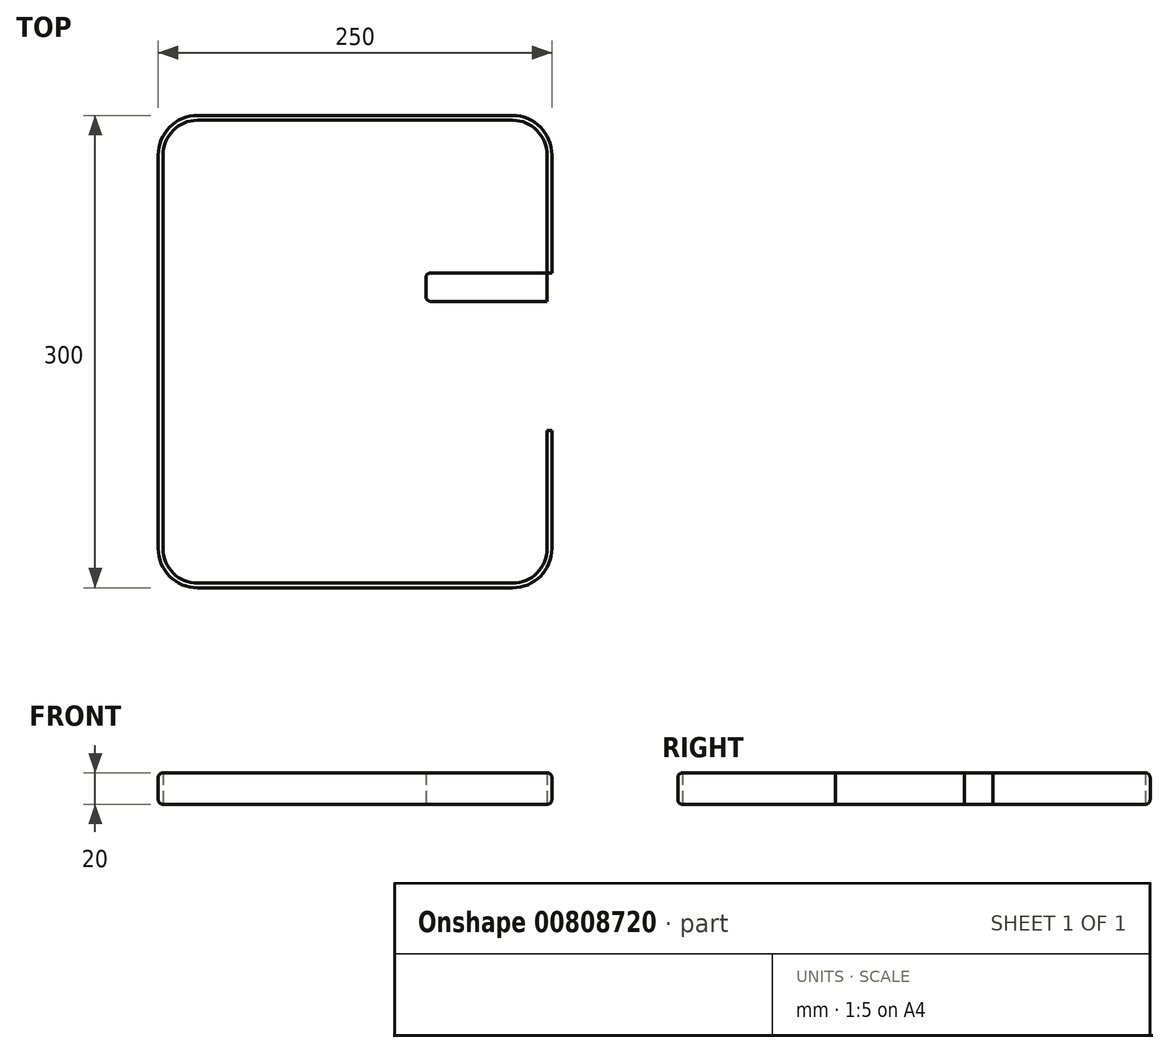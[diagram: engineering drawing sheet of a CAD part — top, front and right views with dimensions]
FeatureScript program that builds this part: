
annotation { "Feature Type Name" : "Feature", "Feature Type Description" : "" }
export const myFeature = defineFeature(function(context is Context, id is Id, definition is map)
    precondition{}
    {
        {
            var Q0;
            Q0=qCreatedBy(makeId("Top.planeOp"),FACE);
            var sketch = newSketch(context, id + "F0", { "sketchPlane" : qUnion([Q0])});
            skLineSegment(sketch, "E0.bottom", {"start": v(100, -150) * mm, "end": v(-100, -150) * mm});
            skLineSegment(sketch, "E0.top", {"start": v(100, 150) * mm, "end": v(-100, 150) * mm});
            skLineSegment(sketch, "E0.left", {"start": v(125, -125) * mm, "end": v(125, 125) * mm});
            skLineSegment(sketch, "E0.right", {"start": v(-125, -125) * mm, "end": v(-125, 125) * mm});
            skPoint(sketch, "E0.middle", {"position": v(0, 0) * mm});
            skPoint(sketch, "E1.visualSharp", {"position": v(-125, 150) * mm});
            skArc(sketch, "E1.filletArc", {"start": v(-100, 150) * mm, "mid": v(-117.68, 142.68) * mm, "end": v(-125, 125) * mm});
            skPoint(sketch, "E2.visualSharp", {"position": v(125, 150) * mm});
            skArc(sketch, "E2.filletArc", {"start": v(125, 125) * mm, "mid": v(117.68, 142.68) * mm, "end": v(100, 150) * mm});
            skPoint(sketch, "E3.visualSharp", {"position": v(125, -150) * mm});
            skArc(sketch, "E3.filletArc", {"start": v(100, -150) * mm, "mid": v(117.68, -142.68) * mm, "end": v(125, -125) * mm});
            skPoint(sketch, "E4.visualSharp", {"position": v(-125, -150) * mm});
            skArc(sketch, "E4.filletArc", {"start": v(-125, -125) * mm, "mid": v(-117.68, -142.68) * mm, "end": v(-100, -150) * mm});
            skSolve(sketch);
        }
        {
            var Q0;
            Q0=makeQuery(id+"F0.imprint","IMPRINT",FACE,{"disambiguationData":[TD([[makeQuery(id+"F0.imprint","IMPRINT",EDGE,{"derivedFrom":sQuery(id+"F0.wireOp",EDGE,"E0.bottom")}),-1.0]])]});
            extrude(context, id + "F1", {"entities" : qUnion([Q0]), "depth" : 20 * mm, "offsetDistance" : 25 * mm});
        }
        {
            var Q0;
            Q0=makeQuery(id+"F1.opExtrude","CAP_FACE",FACE,{"disambiguationData":[OSD([sQuery(id+"F0.wireOp",EDGE,"E0.bottom"),sQuery(id+"F0.wireOp",EDGE,"E0.top"),sQuery(id+"F0.wireOp",EDGE,"E0.left"),sQuery(id+"F0.wireOp",EDGE,"E0.right"),sQuery(id+"F0.wireOp",EDGE,"E1.filletArc"),sQuery(id+"F0.wireOp",EDGE,"E2.filletArc"),sQuery(id+"F0.wireOp",EDGE,"E3.filletArc"),sQuery(id+"F0.wireOp",EDGE,"E4.filletArc")])],"isStart":false});
            var Q1;
            Q1=makeQuery(id+"F1.opExtrude","CAP_FACE",FACE,{"disambiguationData":[OSD([sQuery(id+"F0.wireOp",EDGE,"E0.bottom"),sQuery(id+"F0.wireOp",EDGE,"E0.top"),sQuery(id+"F0.wireOp",EDGE,"E0.left"),sQuery(id+"F0.wireOp",EDGE,"E0.right"),sQuery(id+"F0.wireOp",EDGE,"E1.filletArc"),sQuery(id+"F0.wireOp",EDGE,"E2.filletArc"),sQuery(id+"F0.wireOp",EDGE,"E3.filletArc"),sQuery(id+"F0.wireOp",EDGE,"E4.filletArc")])],"isStart":true});
            fillet(context, id + "F2", {"entities" : qUnion([Q0, Q1]), "radius" : 3 * mm, "tangentPropagation" : true, "allowEdgeOverflow" : false});
        }
        {
            var Q0;
            Q0=makeQuery(id+"F1.opExtrude","CAP_FACE",FACE,{"disambiguationData":[OSD([sQuery(id+"F0.wireOp",EDGE,"E0.bottom"),sQuery(id+"F0.wireOp",EDGE,"E0.top"),sQuery(id+"F0.wireOp",EDGE,"E0.left"),sQuery(id+"F0.wireOp",EDGE,"E0.right"),sQuery(id+"F0.wireOp",EDGE,"E1.filletArc"),sQuery(id+"F0.wireOp",EDGE,"E2.filletArc"),sQuery(id+"F0.wireOp",EDGE,"E3.filletArc"),sQuery(id+"F0.wireOp",EDGE,"E4.filletArc")])],"isStart":true});
            var sketch = newSketch(context, id + "F3", { "sketchPlane" : qUnion([Q0])});
            skLineSegment(sketch, "E5.0", {"start": v(125, 50) * mm, "end": v(125, 32) * mm});
            skLineSegment(sketch, "E6", {"start": v(125, 50) * mm, "end": v(125, 32) * mm, "construction": true});
            skLineSegment(sketch, "E7", {"start": v(48, 32) * mm, "end": v(125, 32) * mm});
            skLineSegment(sketch, "E8", {"start": v(45, 47) * mm, "end": v(45, 35) * mm});
            skLineSegment(sketch, "E9.MirrorCS", {"start": v(48, -32) * mm, "end": v(125, -32) * mm});
            skLineSegment(sketch, "E10.MirrorCS", {"start": v(45, -47) * mm, "end": v(45, -35) * mm});
            skPoint(sketch, "E11.visualSharp", {"position": v(45, 50) * mm});
            skArc(sketch, "E11.filletArc", {"start": v(48, 50) * mm, "mid": v(45.88, 49.12) * mm, "end": v(45, 47) * mm});
            skPoint(sketch, "E12.visualSharp", {"position": v(45, 32) * mm});
            skArc(sketch, "E12.filletArc", {"start": v(45, 35) * mm, "mid": v(45.88, 32.88) * mm, "end": v(48, 32) * mm});
            skLineSegment(sketch, "E13.trimOffspring", {"start": v(125, -32) * mm, "end": v(125, -50) * mm, "construction": true});
            skPoint(sketch, "E14.MirrorCS.end.orphan", {"position": v(45, -50) * mm});
            skPoint(sketch, "E14.MirrorCS.start.orphan", {"position": v(125, -50) * mm});
            skLineSegment(sketch, "E15.trimOffspring", {"start": v(125, -32) * mm, "end": v(125, -50) * mm});
            skPoint(sketch, "E16.orphan", {"position": v(125, 125) * mm});
            skPoint(sketch, "E17.orphan", {"position": v(125, -125) * mm});
            skLineSegment(sketch, "E18", {"start": v(48, 50) * mm, "end": v(125, 50) * mm});
            skLineSegment(sketch, "E19", {"start": v(48, -50) * mm, "end": v(125, -50) * mm});
            skArc(sketch, "E20.MirrorCS", {"start": v(48, -50) * mm, "mid": v(45.88, -49.12) * mm, "end": v(45, -47) * mm});
            skArc(sketch, "E21.MirrorCS", {"start": v(45, -35) * mm, "mid": v(45.88, -32.88) * mm, "end": v(48, -32) * mm});
            skLineSegment(sketch, "E22.MirrorCS", {"start": v(125, -50) * mm, "end": v(125, -32) * mm, "construction": true});
            skPoint(sketch, "E23.orphan", {"position": v(45, -32) * mm});
            skLineSegment(sketch, "E24", {"start": v(45, 35) * mm, "end": v(45, -35) * mm});
            skLineSegment(sketch, "E25", {"start": v(125, -32) * mm, "end": v(125, 32) * mm});
            skSolve(sketch);
        }
        {
            var Q0;
            Q0=makeQuery(id+"F3.imprint","IMPRINT",FACE,{"disambiguationData":[TD([[makeQuery(id+"F3.imprint","IMPRINT",EDGE,{"derivedFrom":sQuery(id+"F3.wireOp",EDGE,"E8")}),1.0]])]});
            var Q1;
            {var subQ0=sQuery(id+"F3.wireOp",EDGE,"E5.0");Q1=makeQuery(id+"F3.imprint","IMPRINT",FACE,{"disambiguationData":[TD([[makeQuery(id+"F3.imprint","IMPRINT",EDGE,{"derivedFrom":subQ0}),-1.0]])]});}
            var Q2;
            {var subQ0=sQuery(id+"F3.wireOp",EDGE,"E15.trimOffspring");Q2=makeQuery(id+"F3.imprint","IMPRINT",FACE,{"disambiguationData":[TD([[makeQuery(id+"F3.imprint","IMPRINT",EDGE,{"derivedFrom":subQ0}),-1.0]])]});}
            var Q3;
            {var subQ1=sQuery(id+"F3.wireOp",EDGE,"E20.MirrorCS");Q3=makeQuery(id+"F3.imprint","IMPRINT",FACE,{"disambiguationData":[TD([[makeQuery(id+"F3.imprint","IMPRINT",EDGE,{"derivedFrom":subQ1}),-1.0]])]});}
            extrude(context, id + "F4", {"entities" : qUnion([Q0, Q1, Q2, Q3]), "operationType" : NewBodyOperationType.REMOVE, "oppositeDirection" : true, "depth" : 25 * mm, "offsetDistance" : 25 * mm});
        }
        {
            var Q0;
            Q0=makeQuery(id+"F4.boolean.opBoolean","COPY",FACE,{"derivedFrom":makeQuery(id+"F4.opExtrude","SWEPT_FACE",FACE,{"disambiguationData":[OSD([sQuery(id+"F3.wireOp",EDGE,"E8")])]})});
            var sketch = newSketch(context, id + "F5", { "sketchPlane" : qUnion([Q0])});
            skPoint(sketch, "E26", {"position": v(-41, 10) * mm});
            skPoint(sketch, "E26.positionSnap0", {"position": v(-41, 20) * mm});
            skPoint(sketch, "E26.positionSnap1", {"position": v(-35, 10) * mm});
            skPoint(sketch, "E27.MirrorP", {"position": v(41, 10) * mm});
            skSolve(sketch);
        }
        {
            var Q0;
            {var subQ5=sQuery(id+"F3.wireOp",EDGE,"E12.filletArc");Q0=makeQuery(id+"F3.imprint","IMPRINT",FACE,{"disambiguationData":[TD([[makeQuery(id+"F3.imprint","IMPRINT",EDGE,{"derivedFrom":subQ5}),-1.0]])]});}
            var sketch = newSketch(context, id + "F6", { "sketchPlane" : qUnion([Q0])});
            skLineSegment(sketch, "E28.0", {"start": v(45, 35) * mm, "end": v(45, -35) * mm});
            skPoint(sketch, "E29.0.end.orphan", {"position": v(45, -35) * mm});
            skPoint(sketch, "E29.0.start.orphan", {"position": v(45, -47) * mm});
            skPoint(sketch, "E30.0.end.orphan", {"position": v(45, 35) * mm});
            skPoint(sketch, "E30.0.start.orphan", {"position": v(45, 47) * mm});
            skArc(sketch, "E31.0", {"start": v(45, 35) * mm, "mid": v(45.88, 32.88) * mm, "end": v(48, 32) * mm});
            skLineSegment(sketch, "E32.0", {"start": v(48, 32) * mm, "end": v(125, 32) * mm});
            skArc(sketch, "E33.0", {"start": v(45, -35) * mm, "mid": v(45.88, -32.88) * mm, "end": v(48, -32) * mm});
            skLineSegment(sketch, "E34.0", {"start": v(48, -32) * mm, "end": v(125, -32) * mm});
            skLineSegment(sketch, "E35.0", {"start": v(125, -32) * mm, "end": v(125, 32) * mm});
            skSolve(sketch);
        }
        {
            var Q0;
            {var subQ5=sQuery(id+"F3.wireOp",EDGE,"E12.filletArc");Q0=makeQuery(id+"F3.imprint","IMPRINT",FACE,{"disambiguationData":[TD([[makeQuery(id+"F3.imprint","IMPRINT",EDGE,{"derivedFrom":subQ5}),-1.0]])]});}
            var Q1;
            {var subQ4=sQuery(id+"F6.wireOp",EDGE,"E35.0");Q1=makeQuery(id+"F6.imprint","IMPRINT",FACE,{"disambiguationData":[TD([[makeQuery(id+"F6.imprint","IMPRINT",EDGE,{"derivedFrom":subQ4}),1.0]])]});}
            extrude(context, id + "F7", {"entities" : qUnion([Q0, Q1]), "operationType" : NewBodyOperationType.REMOVE, "oppositeDirection" : true, "depth" : 25 * mm, "offsetDistance" : 25 * mm});
        }
    });
